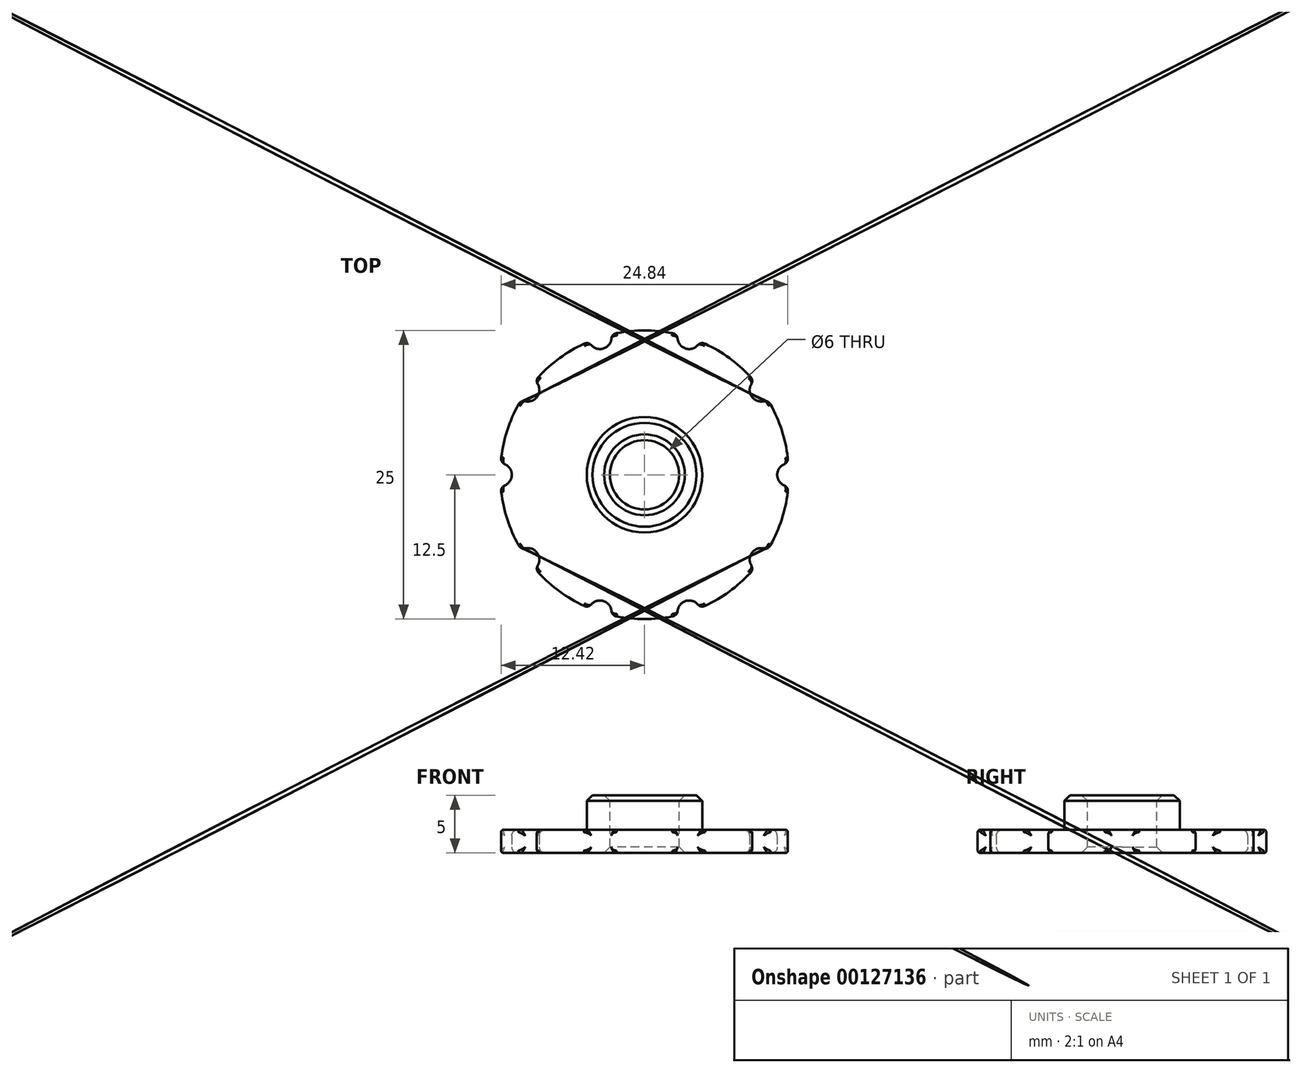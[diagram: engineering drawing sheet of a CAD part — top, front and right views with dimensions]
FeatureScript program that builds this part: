
annotation { "Feature Type Name" : "Feature", "Feature Type Description" : "" }
export const myFeature = defineFeature(function(context is Context, id is Id, definition is map)
    precondition{}
    {
        {
            var Q0;
            Q0=qCreatedBy(makeId("Top.planeOp"),FACE);
            var sketch = newSketch(context, id + "F0", { "sketchPlane" : qUnion([Q0])});
            skCircle(sketch, "E0", {"center": v(0, 0) * mm, "radius": 12.5 * mm});
            skSolve(sketch);
        }
        {
            var Q0;
            Q0=qCreatedBy(makeId("Top.planeOp"),FACE);
            var sketch = newSketch(context, id + "F1", { "sketchPlane" : qUnion([Q0])});
            skCircle(sketch, "E1", {"center": v(12.5, 0) * mm, "radius": 1 * mm});
            skLineSegment(sketch, "E2", {"start": v(0, 0) * mm, "end": v(12.5, 0) * mm, "construction": true});
            skCircle(sketch, "E3.1.0", {"center": v(10.11, 7.35) * mm, "radius": 1 * mm});
            skCircle(sketch, "E3.2.0", {"center": v(3.86, 11.89) * mm, "radius": 1 * mm});
            skCircle(sketch, "E3.3.0", {"center": v(-3.86, 11.89) * mm, "radius": 1 * mm});
            skCircle(sketch, "E3.4.0", {"center": v(-10.11, 7.35) * mm, "radius": 1 * mm});
            skCircle(sketch, "E3.5.0", {"center": v(-12.5, 0) * mm, "radius": 1 * mm});
            skCircle(sketch, "E3.6.0", {"center": v(-10.11, -7.35) * mm, "radius": 1 * mm});
            skCircle(sketch, "E3.7.0", {"center": v(-3.86, -11.89) * mm, "radius": 1 * mm});
            skCircle(sketch, "E3.8.0", {"center": v(3.86, -11.89) * mm, "radius": 1 * mm});
            skCircle(sketch, "E3.9.0", {"center": v(10.11, -7.35) * mm, "radius": 1 * mm});
            skPoint(sketch, "E3.center", {"position": v(0, 0) * mm});
            skSolve(sketch);
        }
        {
            var Q0;
            Q0 = qSketchRegion(id + "F0", true);
            extrude(context, id + "F2", {"entities" : qUnion([Q0]), "depth" : 2 * mm});
        }
        {
            var Q0;
            Q0 = qSketchRegion(id + "F1", true);
            extrude(context, id + "F3", {"entities" : qUnion([Q0]), "operationType" : NewBodyOperationType.REMOVE, "endBound" : BoundingType.THROUGH_ALL, "depth" : 25 * mm});
        }
        {
            var Q0;
            Q0=makeQuery(id+"F2.opExtrude","CAP_FACE",FACE,{"disambiguationData":[OSD([sQuery(id+"F0.wireOp",EDGE,"E0")])],"isStart":false});
            var sketch = newSketch(context, id + "F4", { "sketchPlane" : qUnion([Q0])});
            skCircle(sketch, "E4", {"center": v(0, 0) * mm, "radius": 5 * mm});
            skSolve(sketch);
        }
        {
            var Q0;
            Q0=makeQuery(id+"F4.imprint","IMPRINT",FACE,{"disambiguationData":[TD([[makeQuery(id+"F4.imprint","IMPRINT",EDGE,{"derivedFrom":sQuery(id+"F4.wireOp",EDGE,"E4")}),1.0]])]});
            extrude(context, id + "F5", {"entities" : qUnion([Q0]), "operationType" : NewBodyOperationType.ADD, "depth" : 3 * mm});
        }
        {
            var Q0;
            Q0=makeQuery(id+"F2.opExtrude","CAP_FACE",FACE,{"disambiguationData":[OSD([sQuery(id+"F0.wireOp",EDGE,"E0")])],"isStart":false});
            var sketch = newSketch(context, id + "F6", { "sketchPlane" : qUnion([Q0])});
            skCircle(sketch, "E5", {"center": v(0, 0) * mm, "radius": 3 * mm});
            skSolve(sketch);
        }
        {
            var Q0;
            Q0 = qSketchRegion(id + "F6", true);
            extrude(context, id + "F7", {"entities" : qUnion([Q0]), "operationType" : NewBodyOperationType.REMOVE, "endBound" : BoundingType.THROUGH_ALL, "oppositeDirection" : true, "depth" : 25 * mm, "hasSecondDirection" : true, "secondDirectionBound" : SecondDirectionBoundingType.THROUGH_ALL, "secondDirectionOppositeDirection" : false, "secondDirectionDepth" : 25 * mm});
        }
        {
            var Q0;
            Q0=makeQuery(id+"F7.boolean.opBoolean","INTERSECT",EDGE,{"derivedFrom":[makeQuery(id+"F5.opExtrude","CAP_FACE",FACE,{"disambiguationData":[OSD([sQuery(id+"F4.wireOp",EDGE,"E4")])],"isStart":false}),makeQuery(id+"F7.opExtrude","SWEPT_FACE",FACE,{"disambiguationData":[OSD([sQuery(id+"F6.wireOp",EDGE,"E5")])]})]});
            var Q1;
            Q1=makeQuery(id+"F7.boolean.opBoolean","INTERSECT",EDGE,{"derivedFrom":[makeQuery(id+"F2.opExtrude","CAP_FACE",FACE,{"disambiguationData":[OSD([sQuery(id+"F0.wireOp",EDGE,"E0")])],"isStart":true}),makeQuery(id+"F7.opExtrude","SWEPT_FACE",FACE,{"disambiguationData":[OSD([sQuery(id+"F6.wireOp",EDGE,"E5")])]})]});
            var Q2;
            Q2=makeQuery(id+"F5.opExtrude","CAP_EDGE",EDGE,{"disambiguationData":[OSD([sQuery(id+"F4.wireOp",EDGE,"E4")])],"isStart":false});
            chamfer(context, id + "F8", {"entities" : qUnion([Q0, Q1, Q2]), "width" : 0.5 * mm, "tangentPropagation" : true});
        }
        {
            var Q0;
            Q0=makeQuery(id+"F3.boolean.opBoolean","COPY",FACE,{"derivedFrom":makeQuery(id+"F3.opExtrude","SWEPT_FACE",FACE,{"disambiguationData":[OSD([sQuery(id+"F1.wireOp",EDGE,"E3.8.0")])]})});
            var Q1;
            Q1=makeQuery(id+"F3.boolean.opBoolean","COPY",FACE,{"derivedFrom":makeQuery(id+"F3.opExtrude","SWEPT_FACE",FACE,{"disambiguationData":[OSD([sQuery(id+"F1.wireOp",EDGE,"E3.7.0")])]})});
            var Q2;
            Q2=makeQuery(id+"F3.boolean.opBoolean","COPY",FACE,{"derivedFrom":makeQuery(id+"F3.opExtrude","SWEPT_FACE",FACE,{"disambiguationData":[OSD([sQuery(id+"F1.wireOp",EDGE,"E3.6.0")])]})});
            var Q3;
            Q3=makeQuery(id+"F3.boolean.opBoolean","COPY",FACE,{"derivedFrom":makeQuery(id+"F3.opExtrude","SWEPT_FACE",FACE,{"disambiguationData":[OSD([sQuery(id+"F1.wireOp",EDGE,"E3.5.0")])]})});
            var Q4;
            Q4=makeQuery(id+"F3.boolean.opBoolean","COPY",FACE,{"derivedFrom":makeQuery(id+"F3.opExtrude","SWEPT_FACE",FACE,{"disambiguationData":[OSD([sQuery(id+"F1.wireOp",EDGE,"E3.4.0")])]})});
            var Q5;
            Q5=makeQuery(id+"F3.boolean.opBoolean","COPY",FACE,{"derivedFrom":makeQuery(id+"F3.opExtrude","SWEPT_FACE",FACE,{"disambiguationData":[OSD([sQuery(id+"F1.wireOp",EDGE,"E3.3.0")])]})});
            var Q6;
            Q6=makeQuery(id+"F3.boolean.opBoolean","COPY",FACE,{"derivedFrom":makeQuery(id+"F3.opExtrude","SWEPT_FACE",FACE,{"disambiguationData":[OSD([sQuery(id+"F1.wireOp",EDGE,"E3.2.0")])]})});
            var Q7;
            Q7=makeQuery(id+"F3.boolean.opBoolean","COPY",FACE,{"derivedFrom":makeQuery(id+"F3.opExtrude","SWEPT_FACE",FACE,{"disambiguationData":[OSD([sQuery(id+"F1.wireOp",EDGE,"E3.1.0")])]})});
            var Q8;
            Q8=makeQuery(id+"F3.boolean.opBoolean","COPY",FACE,{"derivedFrom":makeQuery(id+"F3.opExtrude","SWEPT_FACE",FACE,{"disambiguationData":[OSD([sQuery(id+"F1.wireOp",EDGE,"E1")])]})});
            var Q9;
            Q9=makeQuery(id+"F3.boolean.opBoolean","COPY",FACE,{"derivedFrom":makeQuery(id+"F3.opExtrude","SWEPT_FACE",FACE,{"disambiguationData":[OSD([sQuery(id+"F1.wireOp",EDGE,"E3.9.0")])]})});
            fillet(context, id + "F9", {"entities" : qUnion([Q0, Q1, Q2, Q3, Q4, Q5, Q6, Q7, Q8, Q9]), "radius" : 0.5 * mm, "tangentPropagation" : true, "allowEdgeOverflow" : false});
        }
        {
            var Q0;
            Q0=makeQuery(id+"F2.opExtrude","CAP_FACE",FACE,{"disambiguationData":[OSD([sQuery(id+"F0.wireOp",EDGE,"E0")])],"isStart":true});
            var Q1;
            Q1=makeQuery(id+"F2.opExtrude","CAP_FACE",FACE,{"disambiguationData":[OSD([sQuery(id+"F0.wireOp",EDGE,"E0")])],"isStart":false});
            fillet(context, id + "F10", {"entities" : qUnion([Q0, Q1]), "radius" : 0.2 * mm, "tangentPropagation" : true, "allowEdgeOverflow" : false});
        }
    });
